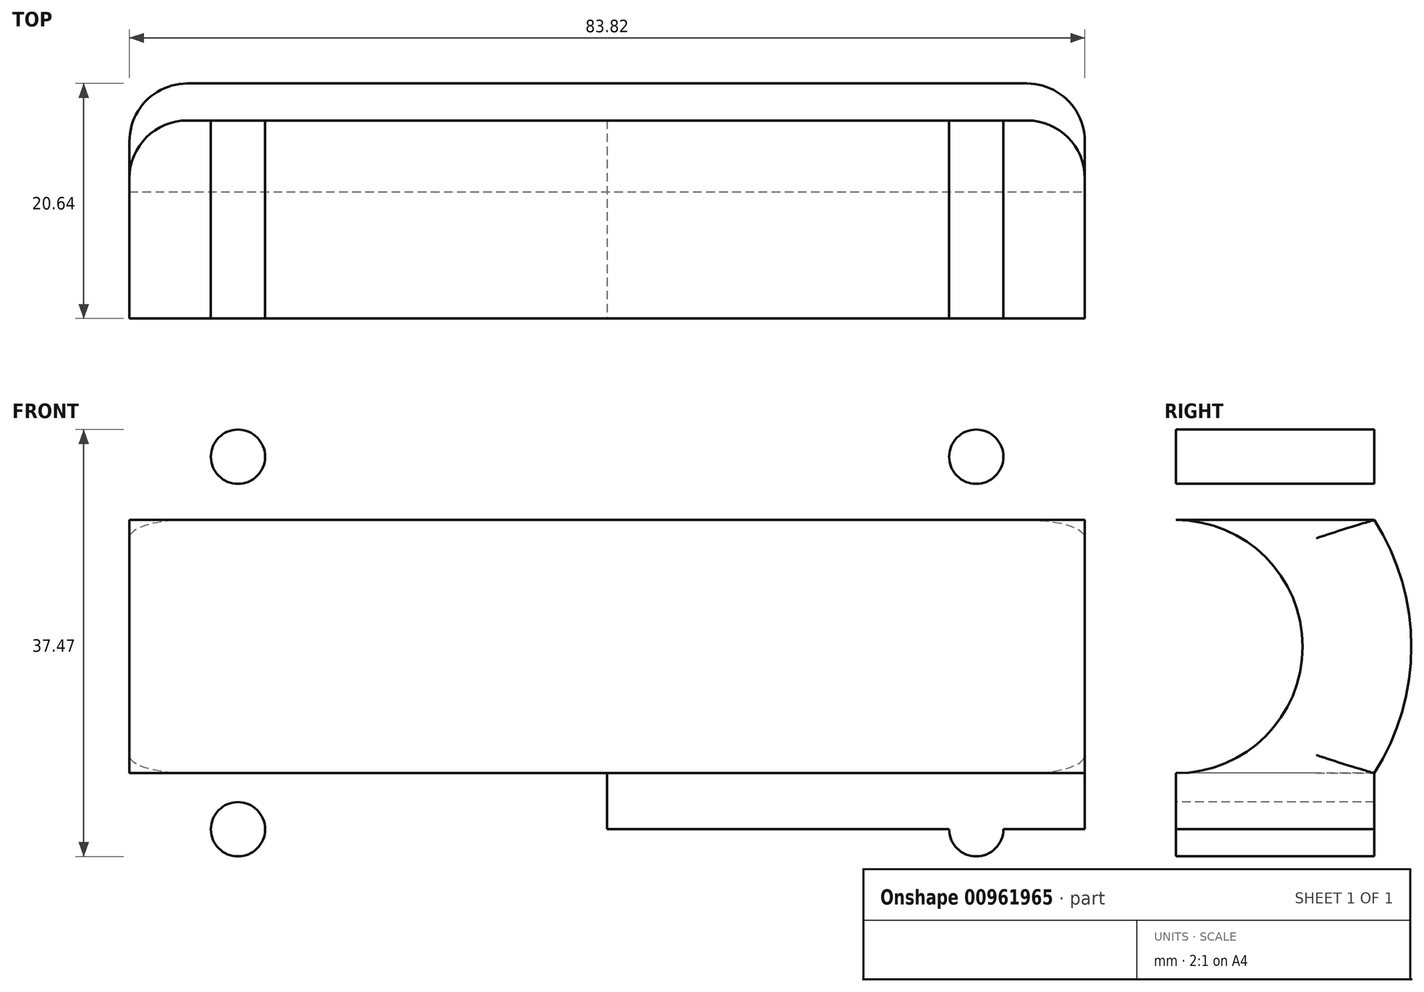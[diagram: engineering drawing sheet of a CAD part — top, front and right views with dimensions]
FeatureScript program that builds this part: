
annotation { "Feature Type Name" : "Feature", "Feature Type Description" : "" }
export const myFeature = defineFeature(function(context is Context, id is Id, definition is map)
    precondition{}
    {
        {
            var Q0;
            Q0=qCreatedBy(makeId("Right.planeOp"),FACE);
            var sketch = newSketch(context, id + "F0", { "sketchPlane" : qUnion([Q0])});
            skCircle(sketch, "E0", {"center": v(0, 0) * mm, "radius": 11.11 * mm});
            skLineSegment(sketch, "E1", {"start": v(0, 0) * mm, "end": v(0, -11.11) * mm});
            skLineSegment(sketch, "E2", {"start": v(0, -11.11) * mm, "end": v(0, 11.11) * mm});
            skLineSegment(sketch, "E3.bottom", {"start": v(0, 11.11) * mm, "end": v(17.4, 11.11) * mm});
            skLineSegment(sketch, "E3.top", {"start": v(0, 22.23) * mm, "end": v(17.4, 22.23) * mm});
            skLineSegment(sketch, "E3.left", {"start": v(0, 11.11) * mm, "end": v(0, 20.64) * mm});
            skLineSegment(sketch, "E3.right", {"start": v(17.4, 11.11) * mm, "end": v(17.4, 22.23) * mm});
            skLineSegment(sketch, "E4.bottom", {"start": v(0, -11.11) * mm, "end": v(17.4, -11.11) * mm});
            skLineSegment(sketch, "E4.top", {"start": v(0, -22.23) * mm, "end": v(17.4, -22.23) * mm});
            skLineSegment(sketch, "E4.left", {"start": v(0, -11.11) * mm, "end": v(0, -20.64) * mm});
            skLineSegment(sketch, "E4.right", {"start": v(17.4, -11.11) * mm, "end": v(17.4, -22.22) * mm});
            skCircle(sketch, "E5.0", {"center": v(0, 0) * mm, "radius": 20.64 * mm});
            skLineSegment(sketch, "E6", {"start": v(0, 20.64) * mm, "end": v(0, 22.23) * mm});
            skLineSegment(sketch, "E7", {"start": v(0, -20.64) * mm, "end": v(0, -22.23) * mm});
            skSolve(sketch);
        }
        {
            var Q0;
            Q0=makeQuery(id+"F0.imprint","IMPRINT",FACE,{"disambiguationData":[TD([[makeQuery(id+"F0.imprint","IMPRINT",EDGE,{"derivedFrom":sQuery(id+"F0.wireOp",EDGE,"E3.top")}),-1.0]])]});
            var Q1;
            Q1=makeQuery(id+"F0.imprint","IMPRINT",FACE,{"disambiguationData":[TD([[makeQuery(id+"F0.imprint","IMPRINT",EDGE,{"derivedFrom":sQuery(id+"F0.wireOp",EDGE,"E4.top")}),1.0]])]});
            var Q2;
            {var subQ3=sQuery(id+"F0.wireOp",EDGE,"E3.bottom");Q2=makeQuery(id+"F0.imprint","IMPRINT",FACE,{"disambiguationData":[TD([[makeQuery(id+"F0.imprint","IMPRINT",EDGE,{"derivedFrom":subQ3}),-1.0]])]});}
            var Q3;
            {var subQ0=sQuery(id+"F0.wireOp",EDGE,"E4.bottom");Q3=makeQuery(id+"F0.imprint","IMPRINT",FACE,{"disambiguationData":[TD([[makeQuery(id+"F0.imprint","IMPRINT",EDGE,{"derivedFrom":subQ0}),-1.0]])]});}
            var Q4;
            {var subQ0=sQuery(id+"F0.wireOp",EDGE,"E3.bottom");Q4=makeQuery(id+"F0.imprint","IMPRINT",FACE,{"disambiguationData":[TD([[makeQuery(id+"F0.imprint","IMPRINT",EDGE,{"derivedFrom":subQ0}),1.0]])]});}
            extrude(context, id + "F1", {"entities" : qUnion([Q0, Q1, Q2, Q3, Q4]), "oppositeDirection" : true, "depth" : 83.82 * mm, "offsetDistance" : 25.4 * mm});
        }
        {
            var Q0;
            Q0=makeQuery(id+"F1.opExtrude","CAP_EDGE",EDGE,{"disambiguationData":[OSD([sQuery(id+"F0.wireOp",EDGE,"E3.right")])],"isStart":true});
            var Q1;
            Q1=makeQuery(id+"F1.opExtrude","CAP_EDGE",EDGE,{"disambiguationData":[OSD([sQuery(id+"F0.wireOp",EDGE,"E4.right")])],"isStart":true});
            var Q2;
            Q2=makeQuery(id+"F1.opExtrude","CAP_EDGE",EDGE,{"disambiguationData":[OSD([sQuery(id+"F0.wireOp",EDGE,"E5.0")])],"isStart":true});
            var Q3;
            Q3=makeQuery(id+"F1.opExtrude","CAP_EDGE",EDGE,{"disambiguationData":[OSD([sQuery(id+"F0.wireOp",EDGE,"E5.0")])],"isStart":false});
            var Q4;
            Q4=makeQuery(id+"F1.opExtrude","CAP_EDGE",EDGE,{"disambiguationData":[OSD([sQuery(id+"F0.wireOp",EDGE,"E3.right")])],"isStart":false});
            var Q5;
            Q5=makeQuery(id+"F1.opExtrude","CAP_EDGE",EDGE,{"disambiguationData":[OSD([sQuery(id+"F0.wireOp",EDGE,"E4.right")])],"isStart":false});
            fillet(context, id + "F2", {"entities" : qUnion([Q0, Q1, Q2, Q3, Q4, Q5]), "radius" : 5.08 * mm, "tangentPropagation" : true, "allowEdgeOverflow" : false});
        }
        {
            var Q0;
            Q0=makeQuery(id+"F1.opExtrude","SWEPT_FACE",FACE,{"disambiguationData":[OSD([sQuery(id+"F0.wireOp",EDGE,"E3.left"),sQuery(id+"F0.wireOp",EDGE,"E6")])]});
            var sketch = newSketch(context, id + "F3", { "sketchPlane" : qUnion([Q0])});
            skLineSegment(sketch, "E8", {"start": v(-41.91, 22.23) * mm, "end": v(-41.91, 11.11) * mm});
            skLineSegment(sketch, "E9", {"start": v(-41.91, 16.67) * mm, "end": v(-83.82, 16.67) * mm});
            skLineSegment(sketch, "E10", {"start": v(-41.91, 16.67) * mm, "end": v(0, 16.67) * mm});
            skCircle(sketch, "E11", {"center": v(-9.53, 16.67) * mm, "radius": 2.38 * mm});
            skCircle(sketch, "E12", {"center": v(-74.3, 16.67) * mm, "radius": 2.38 * mm});
            skSolve(sketch);
        }
        {
            var Q0;
            Q0=makeQuery(id+"F1.opExtrude","SWEPT_FACE",FACE,{"disambiguationData":[OSD([sQuery(id+"F0.wireOp",EDGE,"E4.left"),sQuery(id+"F0.wireOp",EDGE,"E7")])]});
            var sketch = newSketch(context, id + "F4", { "sketchPlane" : qUnion([Q0])});
            skLineSegment(sketch, "E13", {"start": v(-41.91, -11.11) * mm, "end": v(-41.91, -16.03) * mm});
            skLineSegment(sketch, "E14", {"start": v(-41.91, -16.03) * mm, "end": v(0, -16.03) * mm});
            skLineSegment(sketch, "E15", {"start": v(0, -16.03) * mm, "end": v(-41.91, -16.03) * mm});
            skLineSegment(sketch, "E16", {"start": v(-83.82, -16.03) * mm, "end": v(-41.91, -16.03) * mm});
            skCircle(sketch, "E17", {"center": v(-74.3, -16.03) * mm, "radius": 2.38 * mm});
            skCircle(sketch, "E18", {"center": v(-9.53, -16.03) * mm, "radius": 2.38 * mm});
            skSolve(sketch);
        }
        {
            var Q0;
            {var subQ0=sQuery(id+"F3.wireOp",EDGE,"E12");var subQ1=sQuery(id+"F3.wireOp",EDGE,"E9");var subQ2=makeQuery(id+"F3.imprint","INTERSECT",VERTEX,{"disambiguationData":[OD(0.0)],"derivedFrom":[subQ1,subQ0]});Q0=makeQuery(id+"F3.imprint","IMPRINT",FACE,{"disambiguationData":[TD([[makeQuery(id+"F3.imprint","IMPRINT",EDGE,{"disambiguationData":[TD([[subQ2,-1.0]])],"derivedFrom":subQ1}),-1.0]])]});}
            var Q1;
            {var subQ0=sQuery(id+"F3.wireOp",EDGE,"E12");var subQ1=sQuery(id+"F3.wireOp",EDGE,"E9");var subQ2=makeQuery(id+"F3.imprint","INTERSECT",VERTEX,{"disambiguationData":[OD(0.0)],"derivedFrom":[subQ1,subQ0]});Q1=makeQuery(id+"F3.imprint","IMPRINT",FACE,{"disambiguationData":[TD([[makeQuery(id+"F3.imprint","IMPRINT",EDGE,{"disambiguationData":[TD([[subQ2,-1.0]])],"derivedFrom":subQ1}),1.0]])]});}
            var Q2;
            {var subQ0=sQuery(id+"F3.wireOp",EDGE,"E11");var subQ1=sQuery(id+"F3.wireOp",EDGE,"E10");var subQ2=makeQuery(id+"F3.imprint","INTERSECT",VERTEX,{"disambiguationData":[OD(0.0)],"derivedFrom":[subQ1,subQ0]});Q2=makeQuery(id+"F3.imprint","IMPRINT",FACE,{"disambiguationData":[TD([[makeQuery(id+"F3.imprint","IMPRINT",EDGE,{"disambiguationData":[TD([[subQ2,-1.0]])],"derivedFrom":subQ1}),1.0]])]});}
            var Q3;
            {var subQ0=sQuery(id+"F3.wireOp",EDGE,"E11");var subQ1=sQuery(id+"F3.wireOp",EDGE,"E10");var subQ2=makeQuery(id+"F3.imprint","INTERSECT",VERTEX,{"disambiguationData":[OD(0.0)],"derivedFrom":[subQ1,subQ0]});Q3=makeQuery(id+"F3.imprint","IMPRINT",FACE,{"disambiguationData":[TD([[makeQuery(id+"F3.imprint","IMPRINT",EDGE,{"disambiguationData":[TD([[subQ2,-1.0]])],"derivedFrom":subQ1}),-1.0]])]});}
            var Q4;
            {var subQ0=sQuery(id+"F4.wireOp",EDGE,"e8aac25a-046d-4e46-bd20-34a551a780af");var subQ1=sQuery(id+"F4.wireOp",EDGE,"ii2uuSsH-4fu7-3Jdj-W4dM-5R0lmBGjeOV0");var subQ2=makeQuery(id+"F4.imprint","INTERSECT",VERTEX,{"disambiguationData":[OD(0.0)],"derivedFrom":[subQ1,subQ0]});Q4=makeQuery(id+"F4.imprint","IMPRINT",FACE,{"disambiguationData":[TD([[makeQuery(id+"F4.imprint","IMPRINT",EDGE,{"disambiguationData":[TD([[subQ2,-1.0]])],"derivedFrom":subQ1}),1.0]])]});}
            var Q5;
            {var subQ0=sQuery(id+"F4.wireOp",EDGE,"e8aac25a-046d-4e46-bd20-34a551a780af");var subQ1=sQuery(id+"F4.wireOp",EDGE,"ii2uuSsH-4fu7-3Jdj-W4dM-5R0lmBGjeOV0");var subQ2=makeQuery(id+"F4.imprint","INTERSECT",VERTEX,{"disambiguationData":[OD(0.0)],"derivedFrom":[subQ1,subQ0]});Q5=makeQuery(id+"F4.imprint","IMPRINT",FACE,{"disambiguationData":[TD([[makeQuery(id+"F4.imprint","IMPRINT",EDGE,{"disambiguationData":[TD([[subQ2,-1.0]])],"derivedFrom":subQ1}),-1.0]])]});}
            var Q6;
            {var subQ0=sQuery(id+"F4.wireOp",EDGE,"de676944-8c42-4112-840b-95b5a0496836");var subQ1=sQuery(id+"F4.wireOp",EDGE,"WCrA4ssa-xxpD-4Y06-yApS-00h9vAdy05SZ");var subQ2=makeQuery(id+"F4.imprint","INTERSECT",VERTEX,{"disambiguationData":[OD(0.0)],"derivedFrom":[subQ1,subQ0]});Q6=makeQuery(id+"F4.imprint","IMPRINT",FACE,{"disambiguationData":[TD([[makeQuery(id+"F4.imprint","IMPRINT",EDGE,{"disambiguationData":[TD([[subQ2,-1.0]])],"derivedFrom":subQ1}),-1.0]])]});}
            var Q7;
            {var subQ0=sQuery(id+"F4.wireOp",EDGE,"de676944-8c42-4112-840b-95b5a0496836");var subQ1=sQuery(id+"F4.wireOp",EDGE,"WCrA4ssa-xxpD-4Y06-yApS-00h9vAdy05SZ");var subQ2=makeQuery(id+"F4.imprint","INTERSECT",VERTEX,{"disambiguationData":[OD(0.0)],"derivedFrom":[subQ1,subQ0]});Q7=makeQuery(id+"F4.imprint","IMPRINT",FACE,{"disambiguationData":[TD([[makeQuery(id+"F4.imprint","IMPRINT",EDGE,{"disambiguationData":[TD([[subQ2,-1.0]])],"derivedFrom":subQ1}),1.0]])]});}
            extrude(context, id + "F5", {"entities" : qUnion([Q0, Q1, Q2, Q3, Q4, Q5, Q6, Q7]), "operationType" : NewBodyOperationType.REMOVE, "oppositeDirection" : true, "depth" : 25.4 * mm, "offsetDistance" : 25.4 * mm});
        }
        {
            var Q0;
            Q0=makeQuery(id+"F1.opExtrude","SWEPT_EDGE",EDGE,{"disambiguationData":[OSD([sQuery(id+"F0.wireOp",EDGE,"E4.top"),sQuery(id+"F0.wireOp",EDGE,"E4.right")])]});
            var Q1;
            Q1=makeQuery(id+"F1.opExtrude","SWEPT_EDGE",EDGE,{"disambiguationData":[OSD([sQuery(id+"F0.wireOp",EDGE,"E3.top"),sQuery(id+"F0.wireOp",EDGE,"E3.right")])]});
            var Q2;
            Q2=makeQuery(id+"F1.opExtrude","SWEPT_EDGE",EDGE,{"disambiguationData":[OSD([sQuery(id+"F0.wireOp",EDGE,"E4.top"),sQuery(id+"F0.wireOp",EDGE,"E7")])]});
            fillet(context, id + "F6", {"entities" : qUnion([Q0, Q1, Q2]), "radius" : 1.27 * mm, "tangentPropagation" : true, "allowEdgeOverflow" : false});
        }
        {
            var Q0;
            {var subQ0=sQuery(id+"F4.wireOp",EDGE,"E17");var subQ1=sQuery(id+"F4.wireOp",EDGE,"E16");var subQ2=makeQuery(id+"F4.imprint","INTERSECT",VERTEX,{"disambiguationData":[OD(0.0)],"derivedFrom":[subQ1,subQ0]});Q0=makeQuery(id+"F4.imprint","IMPRINT",FACE,{"disambiguationData":[TD([[makeQuery(id+"F4.imprint","IMPRINT",EDGE,{"disambiguationData":[TD([[subQ2,-1.0]])],"derivedFrom":subQ1}),-1.0]])]});}
            var Q1;
            {var subQ0=sQuery(id+"F4.wireOp",EDGE,"E17");var subQ1=sQuery(id+"F4.wireOp",EDGE,"E16");var subQ2=makeQuery(id+"F4.imprint","INTERSECT",VERTEX,{"disambiguationData":[OD(0.0)],"derivedFrom":[subQ1,subQ0]});Q1=makeQuery(id+"F4.imprint","IMPRINT",FACE,{"disambiguationData":[TD([[makeQuery(id+"F4.imprint","IMPRINT",EDGE,{"disambiguationData":[TD([[subQ2,-1.0]])],"derivedFrom":subQ1}),1.0]])]});}
            var Q2;
            {var subQ0=sQuery(id+"F4.wireOp",EDGE,"E18");var subQ1=sQuery(id+"F4.wireOp",EDGE,"E15");var subQ2=makeQuery(id+"F4.imprint","INTERSECT",VERTEX,{"disambiguationData":[OD(0.0)],"derivedFrom":[subQ1,subQ0]});Q2=makeQuery(id+"F4.imprint","IMPRINT",FACE,{"disambiguationData":[TD([[makeQuery(id+"F4.imprint","IMPRINT",EDGE,{"disambiguationData":[TD([[subQ2,-1.0]])],"derivedFrom":subQ1}),1.0]])]});}
            var Q3;
            {var subQ0=sQuery(id+"F4.wireOp",EDGE,"E18");var subQ1=sQuery(id+"F4.wireOp",EDGE,"E15");var subQ2=makeQuery(id+"F4.imprint","INTERSECT",VERTEX,{"disambiguationData":[OD(0.0)],"derivedFrom":[subQ1,subQ0]});Q3=makeQuery(id+"F4.imprint","IMPRINT",FACE,{"disambiguationData":[TD([[makeQuery(id+"F4.imprint","IMPRINT",EDGE,{"disambiguationData":[TD([[subQ2,-1.0]])],"derivedFrom":subQ1}),-1.0]])]});}
            extrude(context, id + "F7", {"entities" : qUnion([Q0, Q1, Q2, Q3]), "operationType" : NewBodyOperationType.REMOVE, "oppositeDirection" : true, "depth" : 25.4 * mm, "offsetDistance" : 25.4 * mm});
        }
    });
